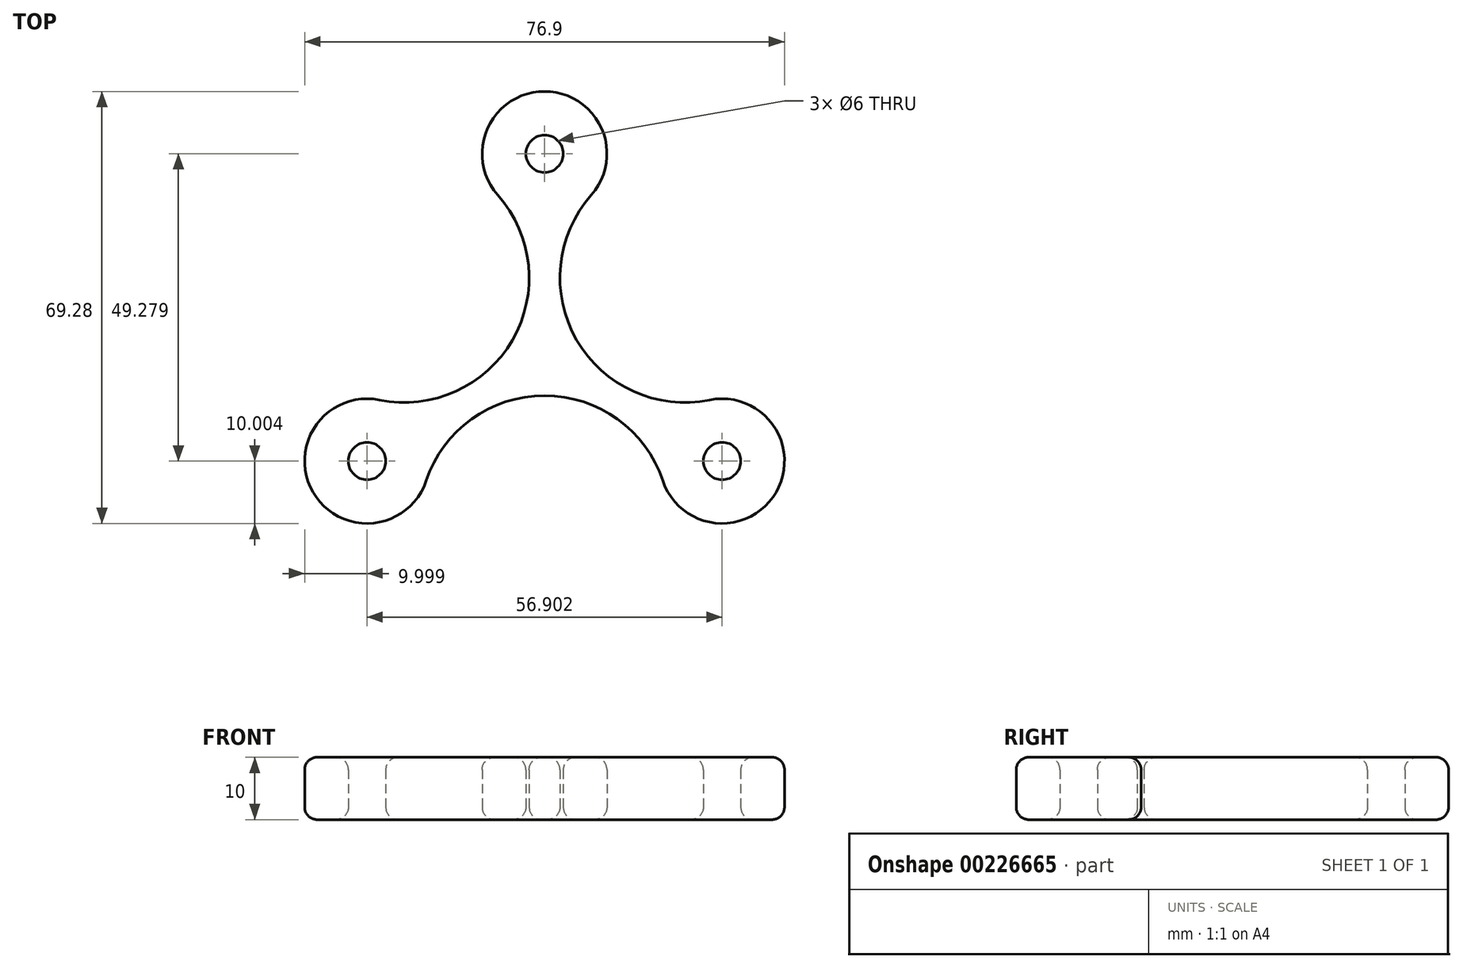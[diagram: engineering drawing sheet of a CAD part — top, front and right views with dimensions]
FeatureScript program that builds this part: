
annotation { "Feature Type Name" : "Feature", "Feature Type Description" : "" }
export const myFeature = defineFeature(function(context is Context, id is Id, definition is map)
    precondition{}
    {
        {
            var Q0;
            Q0=qCreatedBy(makeId("Top.planeOp"),FACE);
            var sketch = newSketch(context, id + "F0", { "sketchPlane" : qUnion([Q0])});
            skLineSegment(sketch, "E0", {"start": v(0, 0) * mm, "end": v(0, 32.85) * mm, "construction": true});
            skLineSegment(sketch, "E1", {"start": v(0, 0) * mm, "end": v(-28.45, -16.43) * mm, "construction": true});
            skLineSegment(sketch, "E2", {"start": v(0, 0) * mm, "end": v(28.45, -16.43) * mm, "construction": true});
            skArc(sketch, "E3", {"start": v(7.49, 26.23) * mm, "mid": v(0, 42.85) * mm, "end": v(-7.49, 26.23) * mm});
            skArc(sketch, "E4", {"start": v(26.46, -6.63) * mm, "mid": v(37.11, -21.43) * mm, "end": v(18.97, -19.6) * mm});
            skArc(sketch, "E5", {"start": v(-18.97, -19.6) * mm, "mid": v(-37.11, -21.43) * mm, "end": v(-26.46, -6.63) * mm});
            skArc(sketch, "E6", {"start": v(-26.46, -6.63) * mm, "mid": v(-5.15, 2.97) * mm, "end": v(-7.49, 26.23) * mm});
            skArc(sketch, "E7", {"start": v(18.97, -19.6) * mm, "mid": v(0, -5.94) * mm, "end": v(-18.97, -19.6) * mm});
            skArc(sketch, "E8", {"start": v(7.49, 26.23) * mm, "mid": v(5.15, 2.97) * mm, "end": v(26.46, -6.63) * mm});
            skSolve(sketch);
        }
        {
            var Q0;
            Q0 = qSketchRegion(id + "F0", true);
            extrude(context, id + "F1", {"entities" : qUnion([Q0]), "depth" : 10 * mm});
        }
        {
            var Q0;
            Q0=qCreatedBy(makeId("Top.planeOp"),FACE);
            var sketch = newSketch(context, id + "F2", { "sketchPlane" : qUnion([Q0])});
            skLineSegment(sketch, "E9.0", {"start": v(0, 0) * mm, "end": v(0, 32.85) * mm, "construction": true});
            skLineSegment(sketch, "E10.0", {"start": v(0, 0) * mm, "end": v(-28.45, -16.43) * mm, "construction": true});
            skLineSegment(sketch, "E11.0", {"start": v(0, 0) * mm, "end": v(28.45, -16.43) * mm, "construction": true});
            skCircle(sketch, "E12", {"center": v(0, 32.85) * mm, "radius": 3 * mm});
            skCircle(sketch, "E13", {"center": v(28.45, -16.43) * mm, "radius": 3 * mm});
            skCircle(sketch, "E14", {"center": v(-28.45, -16.43) * mm, "radius": 3 * mm});
            skSolve(sketch);
        }
        {
            var Q0;
            Q0 = qSketchRegion(id + "F2", true);
            extrude(context, id + "F3", {"entities" : qUnion([Q0]), "operationType" : NewBodyOperationType.REMOVE, "depth" : 25 * mm});
        }
        {
            var Q0;
            Q0=makeQuery(id+"F1.opExtrude","CAP_FACE",FACE,{"disambiguationData":[OSD([sQuery(id+"F0.wireOp",EDGE,"E3"),sQuery(id+"F0.wireOp",EDGE,"E4"),sQuery(id+"F0.wireOp",EDGE,"E5"),sQuery(id+"F0.wireOp",EDGE,"E6"),sQuery(id+"F0.wireOp",EDGE,"E7"),sQuery(id+"F0.wireOp",EDGE,"E8")])],"isStart":false});
            fillet(context, id + "F4", {"entities" : qUnion([Q0]), "radius" : 2 * mm, "tangentPropagation" : true, "allowEdgeOverflow" : false});
        }
        {
            var Q0;
            Q0=makeQuery(id+"F1.opExtrude","CAP_FACE",FACE,{"disambiguationData":[OSD([sQuery(id+"F0.wireOp",EDGE,"E3"),sQuery(id+"F0.wireOp",EDGE,"E4"),sQuery(id+"F0.wireOp",EDGE,"E5"),sQuery(id+"F0.wireOp",EDGE,"E6"),sQuery(id+"F0.wireOp",EDGE,"E7"),sQuery(id+"F0.wireOp",EDGE,"E8")])],"isStart":true});
            fillet(context, id + "F5", {"entities" : qUnion([Q0]), "radius" : 2 * mm, "tangentPropagation" : true, "allowEdgeOverflow" : false});
        }
    });
